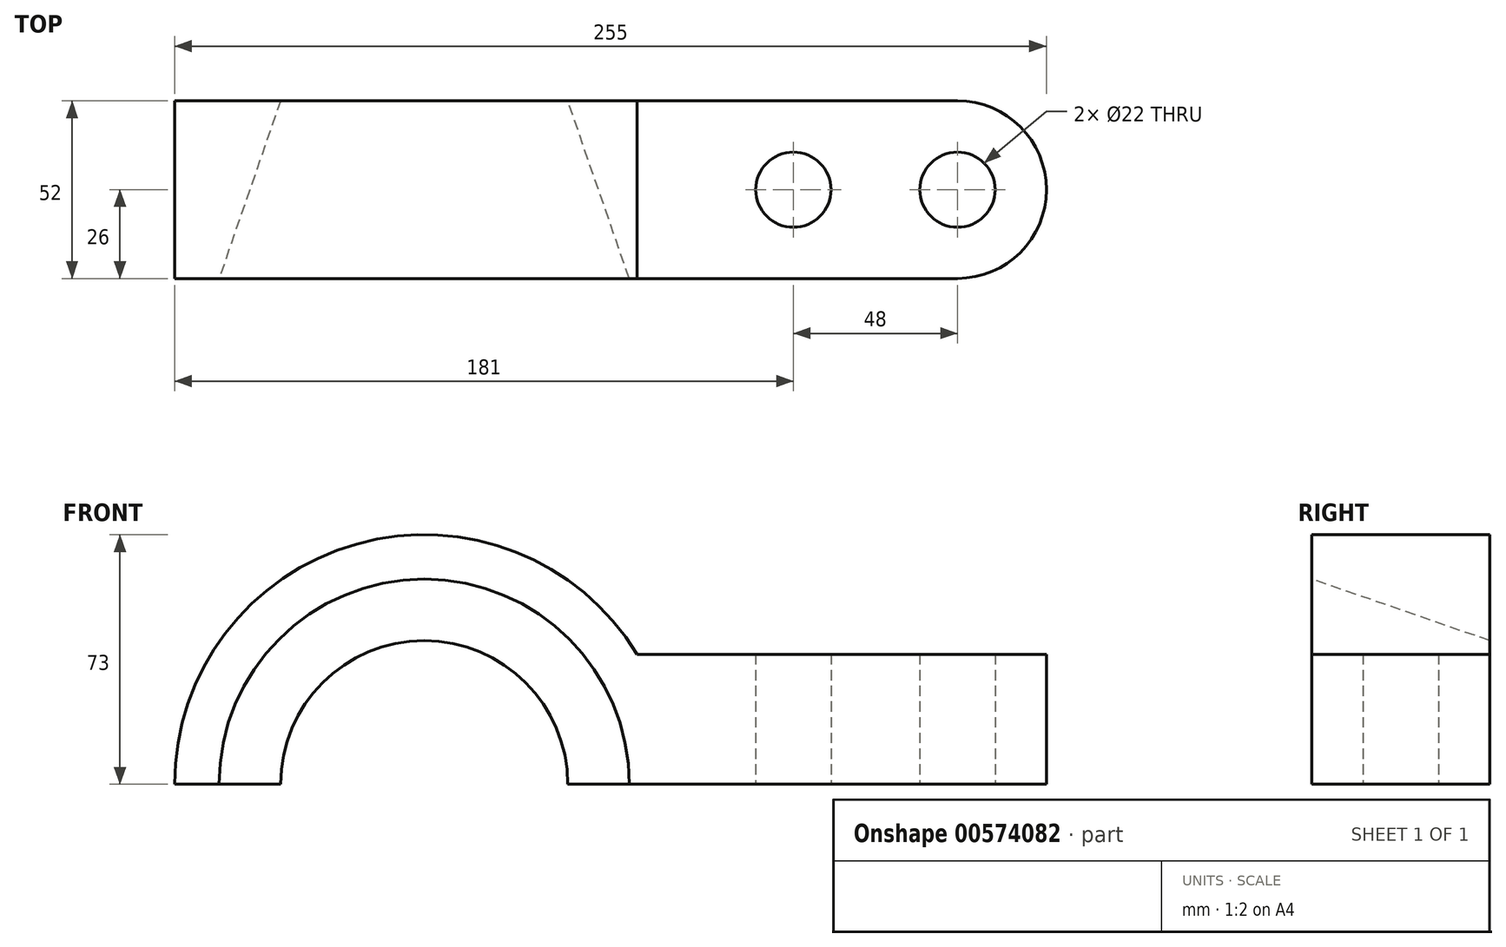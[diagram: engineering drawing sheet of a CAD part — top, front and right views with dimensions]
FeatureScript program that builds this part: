
annotation { "Feature Type Name" : "Feature", "Feature Type Description" : "" }
export const myFeature = defineFeature(function(context is Context, id is Id, definition is map)
    precondition{}
    {
        {
            var Q0;
            Q0=qCreatedBy(makeId("Front.planeOp"),FACE);
            var sketch = newSketch(context, id + "F0", { "sketchPlane" : qUnion([Q0])});
            skLineSegment(sketch, "E0.top", {"start": v(62.33, 38) * mm, "end": v(182, 38) * mm});
            skLineSegment(sketch, "E0.right", {"start": v(182, 0) * mm, "end": v(182, 38) * mm});
            skArc(sketch, "E1", {"start": v(62.33, 38) * mm, "mid": v(-19.73, 70.28) * mm, "end": v(-73, 0) * mm});
            skLineSegment(sketch, "E2", {"start": v(-73, 0) * mm, "end": v(182, 0) * mm});
            skSolve(sketch);
        }
        {
            var Q0;
            Q0 = qSketchRegion(id + "F0", true);
            extrude(context, id + "F1", {"entities" : qUnion([Q0]), "depth" : 52 * mm, "offsetDistance" : 25 * mm});
        }
        {
            var Q0;
            Q0=makeQuery(id+"F1.opExtrude","SWEPT_FACE",FACE,{"disambiguationData":[OSD([sQuery(id+"F0.wireOp",EDGE,"E2")])]});
            var sketch = newSketch(context, id + "F2", { "sketchPlane" : qUnion([Q0])});
            skLineSegment(sketch, "E3", {"start": v(0, 52) * mm, "end": v(0, 0) * mm});
            skLineSegment(sketch, "E4", {"start": v(0, 0) * mm, "end": v(42, 0) * mm});
            skLineSegment(sketch, "E5", {"start": v(42, 0) * mm, "end": v(60, 52) * mm});
            skLineSegment(sketch, "E6", {"start": v(60, 52) * mm, "end": v(0, 52) * mm});
            skSolve(sketch);
        }
        {
            var Q0;
            Q0 = qSketchRegion(id + "F2", true);
            var Q1;
            Q1=sQuery(id+"F2.wireOp",EDGE,"E3");
            revolve(context, id + "F3", {"operationType" : NewBodyOperationType.REMOVE, "entities" : qUnion([Q0]), "axis" : qUnion([Q1]), "revolveType" : RevolveType.FULL, "oppositeDirection" : true});
        }
        {
            var Q0;
            Q0=makeQuery(id+"F1.opExtrude","CAP_EDGE",EDGE,{"disambiguationData":[OSD([sQuery(id+"F0.wireOp",EDGE,"E0.right")])],"isStart":false});
            var Q1;
            Q1=makeQuery(id+"F1.opExtrude","CAP_EDGE",EDGE,{"disambiguationData":[OSD([sQuery(id+"F0.wireOp",EDGE,"E0.right")])],"isStart":true});
            fillet(context, id + "F4", {"entities" : qUnion([Q0, Q1]), "radius" : 26 * mm, "tangentPropagation" : true, "allowEdgeOverflow" : false});
        }
        {
            var Q0;
            {var subQ0=sQuery(id+"F0.wireOp",EDGE,"E2");var subQ2=sQuery(id+"F0.wireOp",EDGE,"E0.right");Q0=makeQuery(id+"F3.boolean.opBoolean","SPLIT",FACE,{"disambiguationData":[TD([makeQuery(id+"F1.opExtrude","SWEPT_FACE",FACE,{"disambiguationData":[OSD([subQ2])]})])],"derivedFrom":makeQuery(id+"F1.opExtrude","SWEPT_FACE",FACE,{"disambiguationData":[OSD([subQ0])]})});}
            var sketch = newSketch(context, id + "F5", { "sketchPlane" : qUnion([Q0])});
            skCircle(sketch, "E7", {"center": v(108, 26) * mm, "radius": 11 * mm});
            skCircle(sketch, "E8", {"center": v(156, 26) * mm, "radius": 11 * mm});
            skSolve(sketch);
        }
        {
            var Q0;
            Q0 = qSketchRegion(id + "F5", true);
            extrude(context, id + "F6", {"entities" : qUnion([Q0]), "operationType" : NewBodyOperationType.REMOVE, "oppositeDirection" : true, "depth" : 92 * mm, "offsetDistance" : 25 * mm});
        }
    });
